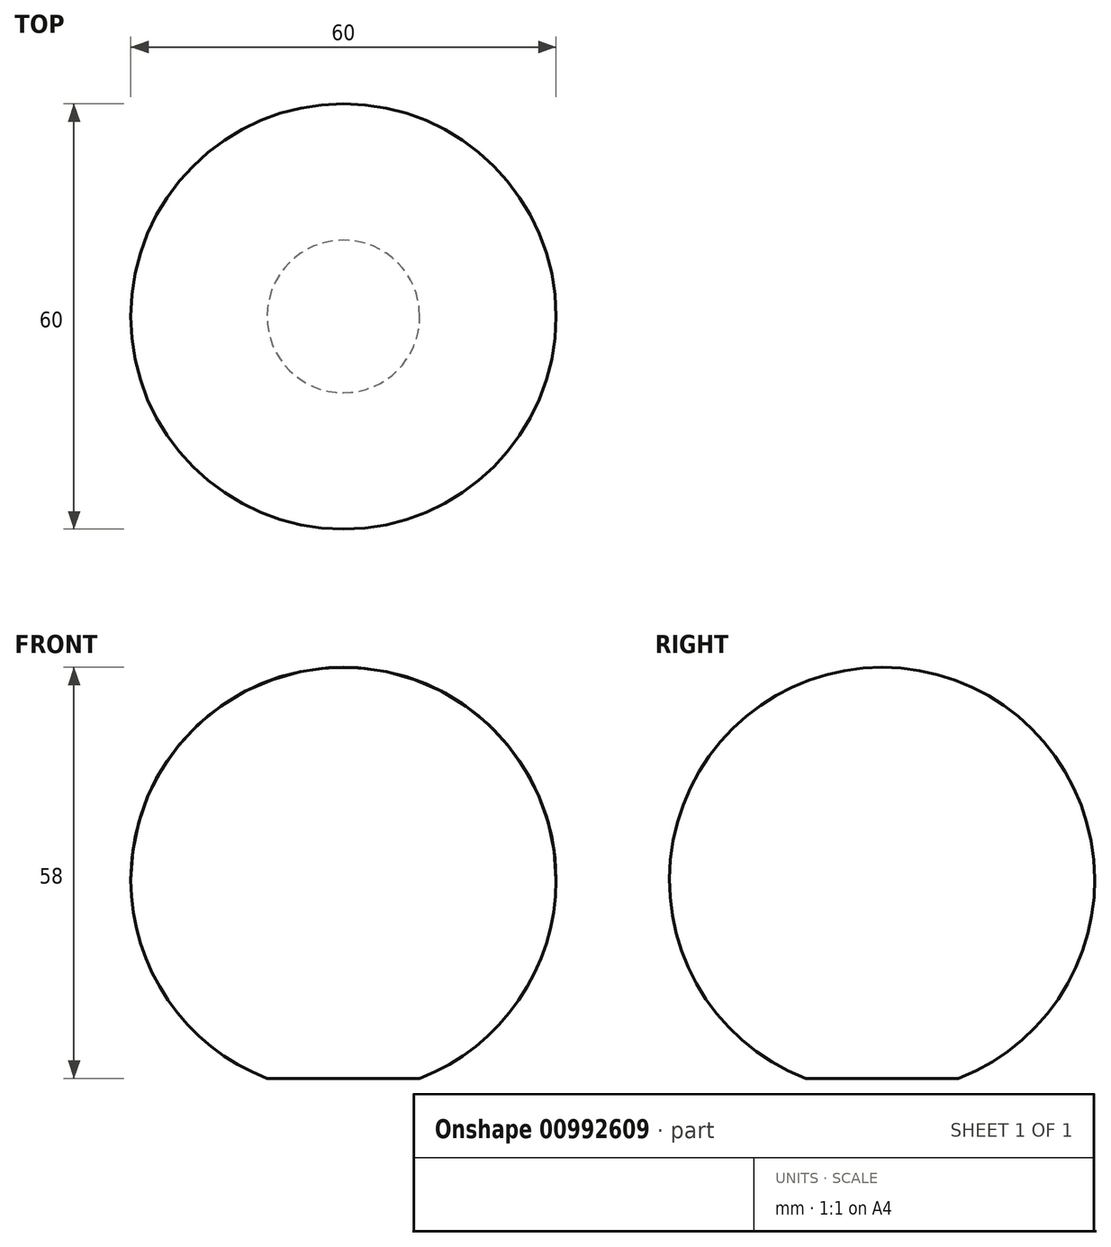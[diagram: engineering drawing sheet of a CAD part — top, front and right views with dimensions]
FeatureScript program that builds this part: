
annotation { "Feature Type Name" : "Feature", "Feature Type Description" : "" }
export const myFeature = defineFeature(function(context is Context, id is Id, definition is map)
    precondition{}
    {
        {
            assignVariable(context, id + "F0", {"name" : "diameter", "anyValue" : 60});
        }
        {
            var Q0;
            Q0=qCreatedBy(makeId("Front.planeOp"),FACE);
            var sketch = newSketch(context, id + "F1", { "sketchPlane" : qUnion([Q0])});
            skArc(sketch, "E0", {"start": v(30, 0) * mm, "mid": v(0, 30) * mm, "end": v(-30, 0) * mm});
            skLineSegment(sketch, "E1", {"start": v(-30, 0) * mm, "end": v(30, 0) * mm});
            skSolve(sketch);
        }
        {
            var Q0;
            Q0=qSketchRegion(id+"F1",true);
            var Q1;
            Q1=sQuery(id+"F1.wireOp",EDGE,"E1");
            revolve(context, id + "F2", {"surfaceOperationType" : NewSurfaceOperationType.NEW, "entities" : qUnion([Q0]), "axis" : qUnion([Q1]), "revolveType" : RevolveType.FULL});
        }
        {
            var Q0;
            Q0=qCreatedBy(makeId("Top.planeOp"),FACE);
            var sketch = newSketch(context, id + "F3", { "sketchPlane" : qUnion([Q0])});
            skLineSegment(sketch, "E2.bottom", {"start": v(-28.02, 29.4) * mm, "end": v(31.98, 29.4) * mm});
            skLineSegment(sketch, "E2.top", {"start": v(-28.02, -30.6) * mm, "end": v(31.98, -30.6) * mm});
            skLineSegment(sketch, "E2.left", {"start": v(-28.02, 29.4) * mm, "end": v(-28.02, -30.6) * mm});
            skLineSegment(sketch, "E2.right", {"start": v(31.98, 29.4) * mm, "end": v(31.98, -30.6) * mm});
            skSolve(sketch);
        }
        {
            var Q0;
            Q0=qSketchRegion(id+"F3",true);
            extrude(context, id + "F4", {"entities" : qUnion([Q0]), "operationType" : NewBodyOperationType.REMOVE, "oppositeDirection" : true, "depth" : 100 * mm, "offsetDistance" : 25 * mm, "hasSecondDirection" : true, "secondDirectionOppositeDirection" : true, "secondDirectionDepth" : ((getVariable(context, 'diameter') / 2) - 2) * mm});
        }
    });
